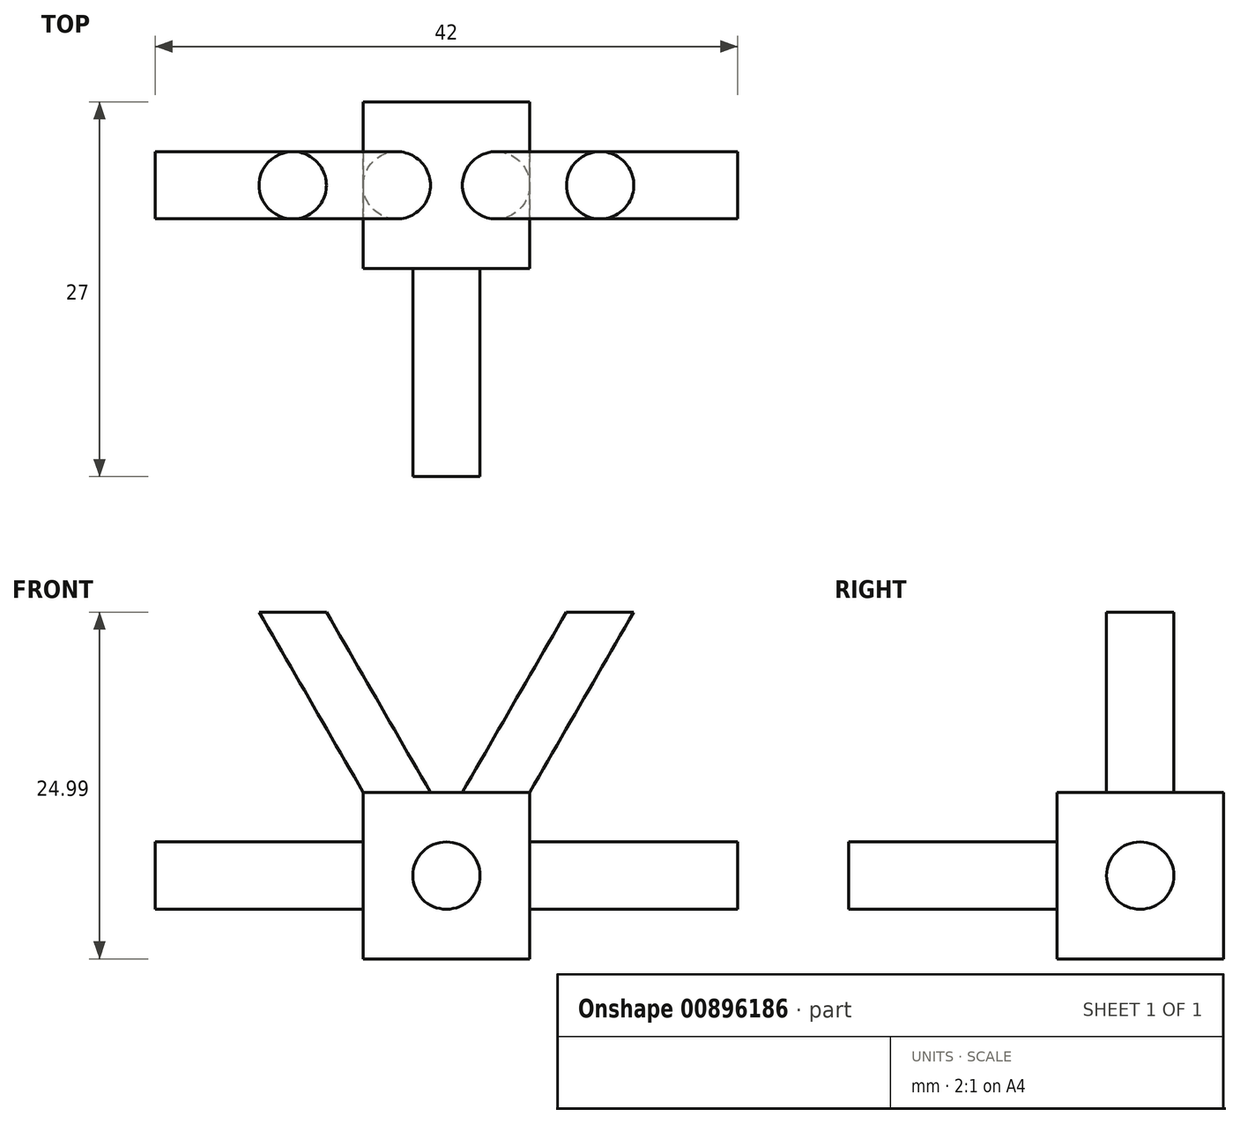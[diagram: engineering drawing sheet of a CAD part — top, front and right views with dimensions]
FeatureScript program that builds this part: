
annotation { "Feature Type Name" : "Feature", "Feature Type Description" : "" }
export const myFeature = defineFeature(function(context is Context, id is Id, definition is map)
    precondition{}
    {
        {
            var Q0;
            Q0=qCreatedBy(makeId("Top.planeOp"),FACE);
            var sketch = newSketch(context, id + "F0", { "sketchPlane" : qUnion([Q0])});
            skLineSegment(sketch, "E0", {"start": v(-22.31, 15.26) * mm, "end": v(-22.31, 3.26) * mm});
            skLineSegment(sketch, "E1", {"start": v(-22.31, 3.26) * mm, "end": v(-10.31, 3.26) * mm});
            skLineSegment(sketch, "E2", {"start": v(-10.31, 3.26) * mm, "end": v(-10.31, 15.26) * mm});
            skLineSegment(sketch, "E3", {"start": v(-10.31, 15.26) * mm, "end": v(-22.31, 15.26) * mm});
            skSolve(sketch);
        }
        {
            var Q0;
            Q0 = qSketchRegion(id + "F0", true);
            extrude(context, id + "F1", {"entities" : qUnion([Q0]), "depth" : 12 * mm, "offsetDistance" : 25 * mm});
        }
        {
            var Q0;
            Q0=makeQuery(id+"F1.opExtrude","SWEPT_FACE",FACE,{"disambiguationData":[OSD([sQuery(id+"F0.wireOp",EDGE,"E2")])]});
            var sketch = newSketch(context, id + "F2", { "sketchPlane" : qUnion([Q0])});
            skCircle(sketch, "E4", {"center": v(9.26, 6) * mm, "radius": 2.43 * mm});
            skSolve(sketch);
        }
        {
            var Q0;
            Q0=makeQuery(id+"F2.imprint","IMPRINT",FACE,{"disambiguationData":[TD([[makeQuery(id+"F2.imprint","IMPRINT",EDGE,{"derivedFrom":sQuery(id+"F2.wireOp",EDGE,"E4")}),1.0]])]});
            extrude(context, id + "F3", {"entities" : qUnion([Q0]), "operationType" : NewBodyOperationType.ADD, "depth" : 15 * mm, "offsetDistance" : 25 * mm});
        }
        {
            var Q0;
            Q0=makeQuery(id+"F1.opExtrude","SWEPT_FACE",FACE,{"disambiguationData":[OSD([sQuery(id+"F0.wireOp",EDGE,"E0")])]});
            var sketch = newSketch(context, id + "F4", { "sketchPlane" : qUnion([Q0])});
            skCircle(sketch, "E5", {"center": v(-9.26, 6) * mm, "radius": 2.43 * mm});
            skSolve(sketch);
        }
        {
            var Q0;
            Q0 = qSketchRegion(id + "F4", true);
            extrude(context, id + "F5", {"entities" : qUnion([Q0]), "operationType" : NewBodyOperationType.ADD, "depth" : 15 * mm, "offsetDistance" : 25 * mm});
        }
        {
            var Q0;
            Q0=makeQuery(id+"F1.opExtrude","SWEPT_FACE",FACE,{"disambiguationData":[OSD([sQuery(id+"F0.wireOp",EDGE,"E1")])]});
            var sketch = newSketch(context, id + "F6", { "sketchPlane" : qUnion([Q0])});
            skCircle(sketch, "E6", {"center": v(-16.31, 6) * mm, "radius": 2.43 * mm});
            skSolve(sketch);
        }
        {
            var Q0;
            Q0 = qSketchRegion(id + "F6", true);
            extrude(context, id + "F7", {"entities" : qUnion([Q0]), "operationType" : NewBodyOperationType.ADD, "depth" : 15 * mm, "offsetDistance" : 25 * mm});
        }
        {
            var Q0;
            Q0=makeQuery(id+"F1.opExtrude","CAP_FACE",FACE,{"disambiguationData":[OSD([sQuery(id+"F0.wireOp",EDGE,"E0"),sQuery(id+"F0.wireOp",EDGE,"E1"),sQuery(id+"F0.wireOp",EDGE,"E2"),sQuery(id+"F0.wireOp",EDGE,"E3")])],"isStart":false});
            var sketch = newSketch(context, id + "F8", { "sketchPlane" : qUnion([Q0])});
            skCircle(sketch, "E7", {"center": v(-19.89, 9.26) * mm, "radius": 2.43 * mm});
            skCircle(sketch, "E8", {"center": v(-12.74, 9.26) * mm, "radius": 2.43 * mm});
            skSolve(sketch);
        }
        {
            var Q0;
            Q0=makeQuery(id+"F1.opExtrude","SWEPT_FACE",FACE,{"disambiguationData":[OSD([sQuery(id+"F0.wireOp",EDGE,"E3")])]});
            var sketch = newSketch(context, id + "F9", { "sketchPlane" : qUnion([Q0])});
            skPoint(sketch, "E9.0", {"position": v(12.74, 12) * mm});
            skPoint(sketch, "E10.0", {"position": v(19.89, 12) * mm});
            skLineSegment(sketch, "E11", {"start": v(19.89, 12) * mm, "end": v(27.39, 25) * mm});
            skLineSegment(sketch, "E12", {"start": v(12.74, 12) * mm, "end": v(5.24, 25) * mm});
            skSolve(sketch);
        }
        {
            var Q0;
            Q0=makeQuery(id+"F8.imprint","IMPRINT",FACE,{"disambiguationData":[TD([[makeQuery(id+"F8.imprint","IMPRINT",EDGE,{"derivedFrom":sQuery(id+"F8.wireOp",EDGE,"E8")}),1.0]])]});
            var Q1;
            Q1=sQuery(id+"F9.wireOp",EDGE,"E12");
            sweep(context, id + "F10", {"operationType" : NewBodyOperationType.ADD, "profiles" : qUnion([Q0]), "path" : qUnion([Q1])});
        }
        {
            var Q0;
            Q0=makeQuery(id+"F8.imprint","IMPRINT",FACE,{"disambiguationData":[TD([[makeQuery(id+"F8.imprint","IMPRINT",EDGE,{"derivedFrom":sQuery(id+"F8.wireOp",EDGE,"E7")}),1.0]])]});
            var Q1;
            Q1=sQuery(id+"F9.wireOp",EDGE,"E11");
            sweep(context, id + "F11", {"operationType" : NewBodyOperationType.ADD, "profiles" : qUnion([Q0]), "path" : qUnion([Q1])});
        }
    });
